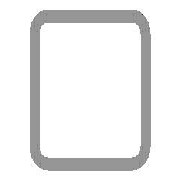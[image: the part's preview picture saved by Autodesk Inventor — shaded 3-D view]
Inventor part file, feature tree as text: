
AUTODESK INVENTOR PART (.ipt)
format: ipt  version: 2025 (Build 290162010, 162A)  size: 135,168 bytes
history: native  units: mm (DEFAULTED — no unit token found)
features: other x4, sketch x1, plane x1
ambient origin geometry x8: Origin, YZ Plane, XZ Plane, XY Plane, X Axis, Y Axis, Z Axis, Center Point
bodies: Solid1 (feature_tree), Body (feature_tree)
feature tree (6):
  parser-record x1  (decoder bookkeeping rows leaked as tree rows — omitted from the tree; the rows remain in map.json)
  other  "Driven Length"
  other  "Start plane"
  other  "End plane"
  sketch  "Sketch3"  dims[d3=2200.0mm d4=0.0mm d7=8.0mm d9=100.0mm d11=100.0mm d12=4.0mm d13=100.0mm d14=2300.0mm d15=50.0mm d16=50.0mm d17=90.0deg d18=2200.0mm]
  plane  "Work Plane3"
